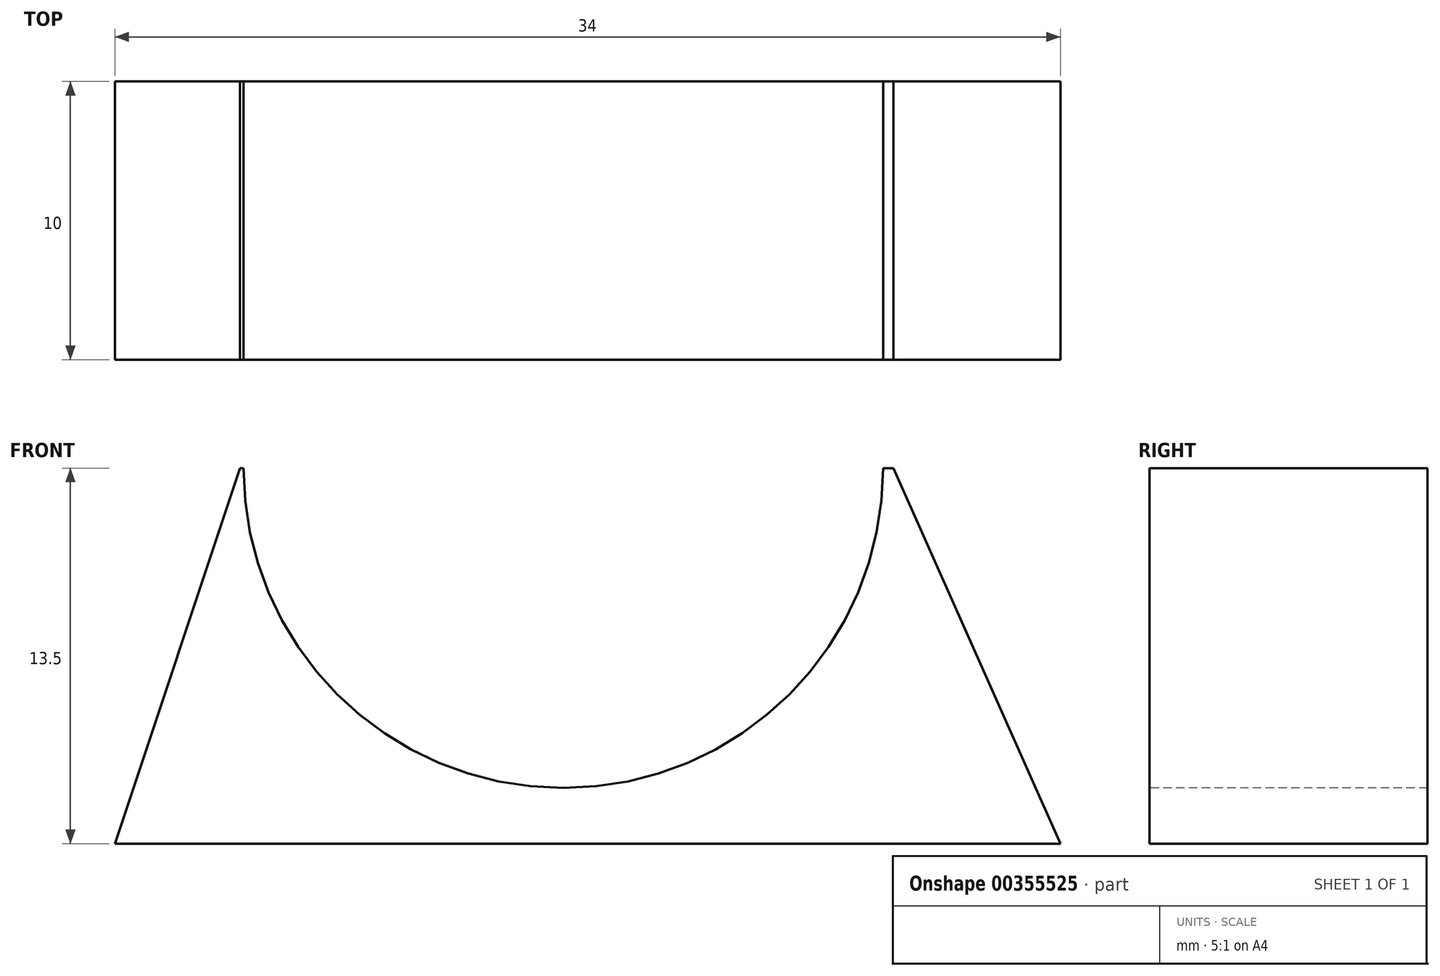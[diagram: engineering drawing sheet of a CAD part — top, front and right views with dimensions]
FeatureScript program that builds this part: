
annotation { "Feature Type Name" : "Feature", "Feature Type Description" : "" }
export const myFeature = defineFeature(function(context is Context, id is Id, definition is map)
    precondition{}
    {
        {
            var Q0;
            Q0=qCreatedBy(makeId("Front.planeOp"),FACE);
            var sketch = newSketch(context, id + "F0", { "sketchPlane" : qUnion([Q0])});
            skLineSegment(sketch, "E0.bottom", {"start": v(-17, -6.75) * mm, "end": v(17, -6.75) * mm});
            skLineSegment(sketch, "E0.top", {"start": v(-17, 6.75) * mm, "end": v(17, 6.75) * mm});
            skLineSegment(sketch, "E0.left", {"start": v(-17, -6.75) * mm, "end": v(-17, 6.75) * mm});
            skLineSegment(sketch, "E0.right", {"start": v(17, -6.75) * mm, "end": v(17, 6.75) * mm});
            skPoint(sketch, "E0.middle", {"position": v(0, 0) * mm});
            skSolve(sketch);
        }
        {
            var Q0;
            Q0 = qSketchRegion(id + "F0", true);
            extrude(context, id + "F1", {"entities" : qUnion([Q0]), "oppositeDirection" : true, "depth" : 10 * mm});
        }
        {
            var Q0;
            Q0=makeQuery(id+"F1.opExtrude","CAP_FACE",FACE,{"disambiguationData":[OSD([sQuery(id+"F0.wireOp",EDGE,"E0.bottom"),sQuery(id+"F0.wireOp",EDGE,"E0.top"),sQuery(id+"F0.wireOp",EDGE,"E0.left"),sQuery(id+"F0.wireOp",EDGE,"E0.right")])],"isStart":true});
            var sketch = newSketch(context, id + "F2", { "sketchPlane" : qUnion([Q0])});
            skLineSegment(sketch, "E1", {"start": v(-12.5, 6.75) * mm, "end": v(-17, -6.75) * mm});
            skLineSegment(sketch, "E2", {"start": v(11, 6.75) * mm, "end": v(17, -6.75) * mm});
            skCircle(sketch, "E3", {"center": v(-0.88, 6.75) * mm, "radius": 11.5 * mm});
            skSolve(sketch);
        }
        {
            var Q0;
            Q0 = qSketchRegion(id + "F2", true);
            var Q1;
            {var subQ0=sQuery(id+"F2.wireOp",EDGE,"E1");Q1=makeQuery(id+"F2.imprint","IMPRINT",FACE,{"disambiguationData":[TD([[makeQuery(id+"F2.imprint","IMPRINT",EDGE,{"derivedFrom":subQ0}),-1.0]])]});}
            var Q2;
            {var subQ0=sQuery(id+"F2.wireOp",EDGE,"E2");Q2=makeQuery(id+"F2.imprint","IMPRINT",FACE,{"disambiguationData":[TD([[makeQuery(id+"F2.imprint","IMPRINT",EDGE,{"derivedFrom":subQ0}),1.0]])]});}
            extrude(context, id + "F3", {"entities" : qUnion([Q0, Q1, Q2]), "operationType" : NewBodyOperationType.REMOVE, "endBound" : BoundingType.THROUGH_ALL, "oppositeDirection" : true, "depth" : 25 * mm});
        }
    });
